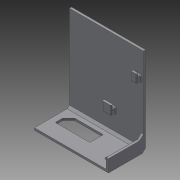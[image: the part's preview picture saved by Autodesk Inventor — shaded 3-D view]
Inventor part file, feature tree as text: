
AUTODESK INVENTOR PART (.ipt)
format: ipt  version: 2015 SP1 (Build 190203100, 203)  size: 217,088 bytes
history: native  units: mm
features: extrude x5, sketch x5, chamfer x4, fillet x2, plane x2
ambient origin geometry x8: Origin, YZ Plane, XZ Plane, XY Plane, X Axis, Y Axis, Z Axis, Center Point
bodies: Solid1 (feature_tree)
feature tree (18):
  extrude  "Extrusion1"  Depth=47.0mm
  extrude  "Extrusion2"  Depth=18.65mm TaperAngle=0.0deg
  chamfer  "Chamfer1"  Distance=1.15mm Angle=45.0deg
  chamfer  "Chamfer3"  Distance=2.0mm Angle=45.0deg
  extrude  "Extrusion3"  TaperAngle=135.0deg  [1 undecoded]
  chamfer  "Chamfer4"  Angle=135.0deg  [1 undecoded]
  chamfer  "Chamfer5"  Distance=18.5mm
  fillet  "Fillet1"  Radius=7.2mm
  plane  "Work Plane1"
  extrude  "Extrusion4"  Depth=2.5mm
  plane  "Work Plane2"
  extrude  "Extrusion5"  Depth=2.5mm
  fillet  "Fillet4"  Radius=8.0mm
  sketch  "Sketch1"  dims[d0=39.5mm d1=47.0mm]
  sketch  "Sketch2"  dims[d2=1.15mm d3=0.0mm d4=18.65mm d5=0.0mm]
  sketch  "Sketch3"  dims[d7=6.6mm]
  sketch  "Sketch5"  dims[d9=1.15mm d10=1.15mm d11=2.0mm d12=45.0deg d16=1.75mm d17=2.0mm d18=45.0deg]
  sketch  "Sketch6"  dims[d19=2.7mm d21=135.0deg d22=135.0deg d24=18.5mm d25=7.2mm d34=5.5mm d35=5.5mm d36=8.0mm d38=1.15mm d39=0.0mm d40=2.0mm d41=2.0mm d42=45.0deg d43=3.1mm d44=1.5mm d45=0.75mm d46=45.0deg d47=4.0mm d48=0.5mm d49=-1.25mm d50=3.0mm d51=0.0mm d52=4.8mm d55=1.5mm d57=31.0mm d58=3.0mm d60=0.5mm d61=-14.8mm d62=5.0mm d63=2.0mm d64=2.5mm d66=4.75mm d67=0.0mm d68=9.5mm d69=1.4mm d70=2.5mm]
note: 2 required parameter values undecoded (feature->parameter linkage not recoverable at this tier; creation-order binding heuristic only, values carry confidence <= 0.55)
